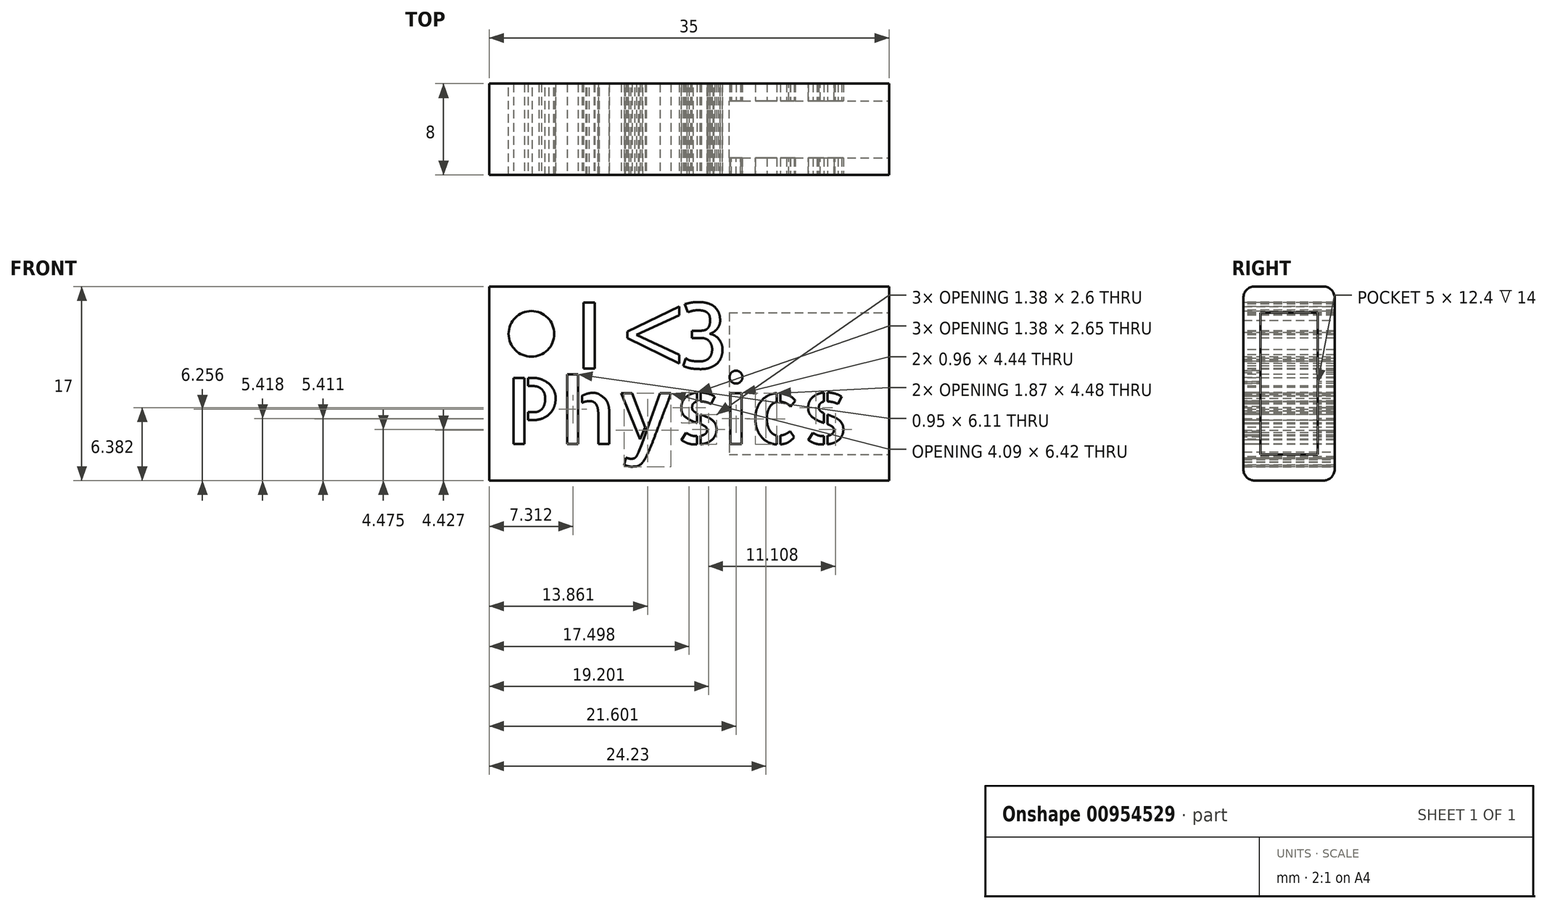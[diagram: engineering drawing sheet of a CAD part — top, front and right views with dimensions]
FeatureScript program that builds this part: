
annotation { "Feature Type Name" : "Feature", "Feature Type Description" : "" }
export const myFeature = defineFeature(function(context is Context, id is Id, definition is map)
    precondition{}
    {
        {
            var Q0;
            Q0=qCreatedBy(makeId("Top.planeOp"),FACE);
            var sketch = newSketch(context, id + "F0", { "sketchPlane" : qUnion([Q0])});
            skLineSegment(sketch, "E0.bottom", {"start": v(-7.5, 4) * mm, "end": v(7.5, 4) * mm});
            skLineSegment(sketch, "E0.top", {"start": v(-7.5, -4) * mm, "end": v(7.5, -4) * mm});
            skLineSegment(sketch, "E0.left", {"start": v(-8.5, 3) * mm, "end": v(-8.5, -3) * mm});
            skLineSegment(sketch, "E0.right", {"start": v(8.5, 3) * mm, "end": v(8.5, -3) * mm});
            skPoint(sketch, "E0.middle", {"position": v(0, 0) * mm});
            skPoint(sketch, "E1.visualSharp", {"position": v(-8.5, 4) * mm});
            skArc(sketch, "E1.filletArc", {"start": v(-7.5, 4) * mm, "mid": v(-8.2, 3.7) * mm, "end": v(-8.5, 3) * mm});
            skPoint(sketch, "E2.visualSharp", {"position": v(8.5, 4) * mm});
            skArc(sketch, "E2.filletArc", {"start": v(8.5, 3) * mm, "mid": v(8.2, 3.7) * mm, "end": v(7.5, 4) * mm});
            skPoint(sketch, "E3.visualSharp", {"position": v(8.5, -4) * mm});
            skArc(sketch, "E3.filletArc", {"start": v(7.5, -4) * mm, "mid": v(8.2, -3.7) * mm, "end": v(8.5, -3) * mm});
            skPoint(sketch, "E4.visualSharp", {"position": v(-8.5, -4) * mm});
            skArc(sketch, "E4.filletArc", {"start": v(-8.5, -3) * mm, "mid": v(-8.2, -3.7) * mm, "end": v(-7.5, -4) * mm});
            skSolve(sketch);
        }
        {
            var Q0;
            Q0 = qSketchRegion(id + "F0", true);
            extrude(context, id + "F1", {"entities" : qUnion([Q0]), "depth" : 35 * mm, "offsetDistance" : 25 * mm});
        }
        {
            var Q0;
            Q0=makeQuery(id+"F1.opExtrude","CAP_FACE",FACE,{"disambiguationData":[OSD([sQuery(id+"F0.wireOp",EDGE,"E0.bottom"),sQuery(id+"F0.wireOp",EDGE,"E0.top"),sQuery(id+"F0.wireOp",EDGE,"E0.left"),sQuery(id+"F0.wireOp",EDGE,"E0.right"),sQuery(id+"F0.wireOp",EDGE,"E1.filletArc"),sQuery(id+"F0.wireOp",EDGE,"E2.filletArc"),sQuery(id+"F0.wireOp",EDGE,"E3.filletArc"),sQuery(id+"F0.wireOp",EDGE,"E4.filletArc")])],"isStart":true});
            var sketch = newSketch(context, id + "F2", { "sketchPlane" : qUnion([Q0])});
            skLineSegment(sketch, "E5.bottom", {"start": v(6.2, 2.5) * mm, "end": v(-6.2, 2.5) * mm});
            skLineSegment(sketch, "E5.top", {"start": v(6.2, -2.5) * mm, "end": v(-6.2, -2.5) * mm});
            skLineSegment(sketch, "E5.left", {"start": v(6.2, 2.5) * mm, "end": v(6.2, -2.5) * mm});
            skLineSegment(sketch, "E5.right", {"start": v(-6.2, 2.5) * mm, "end": v(-6.2, -2.5) * mm});
            skPoint(sketch, "E5.middle", {"position": v(0, 0) * mm});
            skSolve(sketch);
        }
        {
            var Q0;
            Q0 = qSketchRegion(id + "F2", true);
            extrude(context, id + "F3", {"entities" : qUnion([Q0]), "operationType" : NewBodyOperationType.REMOVE, "oppositeDirection" : true, "depth" : 14 * mm, "offsetDistance" : 25 * mm});
        }
        {
            var Q0;
            Q0=makeQuery(id+"F1.opExtrude","SWEPT_BODY",BODY,{"disambiguationData":[OSD([sQuery(id+"F0.wireOp",EDGE,"E0.bottom"),sQuery(id+"F0.wireOp",EDGE,"E0.top"),sQuery(id+"F0.wireOp",EDGE,"E0.left"),sQuery(id+"F0.wireOp",EDGE,"E0.right"),sQuery(id+"F0.wireOp",EDGE,"E1.filletArc"),sQuery(id+"F0.wireOp",EDGE,"E2.filletArc"),sQuery(id+"F0.wireOp",EDGE,"E3.filletArc"),sQuery(id+"F0.wireOp",EDGE,"E4.filletArc")])]});
            var Q1;
            Q1=makeQuery(id+"F1.opExtrude","CAP_EDGE",EDGE,{"disambiguationData":[OSD([sQuery(id+"F0.wireOp",EDGE,"E0.right")])],"isStart":true});
            transform(context, id + "F4", {"entities" : qUnion([Q0]), "transformType" : TransformType.ROTATION, "transformAxis" : qUnion([Q1]), "angle" : 90 * degree, "makeCopy" : false});
        }
        {
            var Q0;
            Q0=makeQuery(id+"F1.opExtrude","SWEPT_FACE",FACE,{"disambiguationData":[OSD([sQuery(id+"F0.wireOp",EDGE,"E0.top")])]});
            var sketch = newSketch(context, id + "F5", { "sketchPlane" : qUnion([Q0])});
            skText(sketch, "E6", { "text": "I   3", "fontName": "AllertaStencil-Regular.ttf"});
            const initialGuessF5  = {"E6": [-0.01898, -0.0072, 1, 0, 0.0058]};
            skSetInitialGuess(sketch, initialGuessF5);
            skSolve(sketch);
        }
        {
            var Q0;
            Q0 = qSketchRegion(id + "F5", true);
            extrude(context, id + "F6", {"entities" : qUnion([Q0]), "operationType" : NewBodyOperationType.REMOVE, "oppositeDirection" : true, "depth" : 8 * mm, "offsetDistance" : 25 * mm});
        }
        {
            var Q0;
            Q0=makeQuery(id+"F1.opExtrude","SWEPT_FACE",FACE,{"disambiguationData":[OSD([sQuery(id+"F0.wireOp",EDGE,"E0.bottom")])]});
            var sketch = newSketch(context, id + "F7", { "sketchPlane" : qUnion([Q0])});
            skCircle(sketch, "E7", {"center": v(22.81, -4.15) * mm, "radius": 2 * mm});
            skSolve(sketch);
        }
        {
            var Q0;
            Q0 = qSketchRegion(id + "F7", true);
            extrude(context, id + "F8", {"entities" : qUnion([Q0]), "operationType" : NewBodyOperationType.REMOVE, "oppositeDirection" : true, "depth" : 8 * mm, "offsetDistance" : 25 * mm});
        }
        {
            var Q0;
            Q0=makeQuery(id+"F1.opExtrude","SWEPT_FACE",FACE,{"disambiguationData":[OSD([sQuery(id+"F0.wireOp",EDGE,"E0.top")])]});
            var sketch = newSketch(context, id + "F9", { "sketchPlane" : qUnion([Q0])});
            skText(sketch, "E8", { "text": "Physics", "fontName": "AllertaStencil-Regular.ttf"});
            const initialGuessF9  = {"E8": [-0.0251, -0.0138, 1, 0, 0.0058]};
            skSetInitialGuess(sketch, initialGuessF9);
            skSolve(sketch);
        }
        {
            var Q0;
            Q0 = qSketchRegion(id + "F9", true);
            extrude(context, id + "F10", {"entities" : qUnion([Q0]), "operationType" : NewBodyOperationType.REMOVE, "oppositeDirection" : true, "depth" : 8 * mm, "offsetDistance" : 25 * mm});
        }
        {
            var Q0;
            Q0=makeQuery(id+"F1.opExtrude","SWEPT_FACE",FACE,{"disambiguationData":[OSD([sQuery(id+"F0.wireOp",EDGE,"E0.top")])]});
            var sketch = newSketch(context, id + "F11", { "sketchPlane" : qUnion([Q0])});
            skText(sketch, "E9", { "text": "<", "fontName": "AllertaStencil-Regular.ttf"});
            const initialGuessF11  = {"E9": [-0.01467, -0.0067, 1, 0, 0.0063]};
            skSetInitialGuess(sketch, initialGuessF11);
            skSolve(sketch);
        }
        {
            var Q0;
            Q0 = qSketchRegion(id + "F11", true);
            extrude(context, id + "F12", {"entities" : qUnion([Q0]), "operationType" : NewBodyOperationType.REMOVE, "oppositeDirection" : true, "depth" : 8 * mm, "offsetDistance" : 25 * mm});
        }
    });
